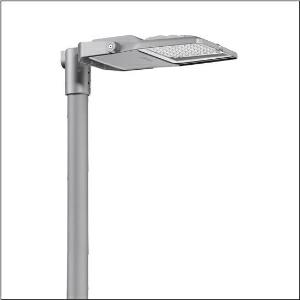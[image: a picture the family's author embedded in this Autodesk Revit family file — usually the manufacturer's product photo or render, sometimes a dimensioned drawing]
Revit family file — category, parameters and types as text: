
# Revit family: floodlight_fl_21_mini___pl33t_5xa7776d2f3a_276e
name_source: partatom
category: Lighting Fixtures
units: mm (PartAtom-declared; Revit-internal decimal feet)

## family parameters
Cut with Voids When Loaded = No
Host = Face
Light Source = No
Part Type = Normal
Room Calculation Point = No
Round Connector Dimension = Use Diameter
Shared = No

## types (1)
- --- (1 x LED, 17630 lm, 142.9 W, 3000K)
    Apparent Load = 143 VA
    CIE Flux Codes = 26 75 99 100 100
    Color Rendering = 70
    Color Temperature = 3000K
    Default Elevation = 1800 mm
    Description = Floodlight FL 21 mini, floodlight, primary light control with lens, of PMMA, primary optical cover: protective disc, of toughened safety glass, transparent, light distribution: PL33T, light emission: direct distribution, installation type: surface-mounted, LED, High Power LED, rated luminous flux: 17.630lm, luminous efficacy: 123lm/W, light colour: 730, colour temperature: 3000K, control: flexible luminous flux parameterisation, time-dependent luminous flux control, constant luminous flux control, overheat protection, presetting dimming logarithmic, with terminal, 6-pole, mains connection: 220..240V, AC, 50/60Hz, start of lifetime: 143W, end of service life: 151W, reduction: 63W, luminaire housing, of diecast aluminium, powder-coated, Siteco® metallic grey (DB 702S), corrosivity category C5 mid according to DIN EN ISO 12944, sealing non-destructively replaceable, please order mast flange separately, mast bracket, of steel, galvanised, powder-coated, Siteco® metallic grey (DB 702S), Smart Interface below and above, protection rating (complete): IP66, insulation class (complete): insulation class II (safety insulation), certification: CE, ENEC, VDE, protection symbol: D, impact resistance: IK08, permissible operating ambient temperature: -40..+40°C, permissible operating ambient temperature for outdoor applications: -40..+50°C, standard: DIN EN 12944, LABS conformity tested according to VDMA 24364:2018-05, packaging unit: 1 piece

Light Distribution: PL33T
    Height = 70 mm
    Lamp = 1 x LED
    Lamp Light Flux = 17630 lm
    Lamp Power = 142.9 W
    Lamp count = 1
    Length = 485 mm
    Luminous efficacy = 123 lm/W
    Manufacturer = Siteco
    ModVariant = No
    Model = 5XA7776D2F3A
    Number of Poles = 1
    OnlyDefault = Yes
    Power Factor = 1
    Product Name = Floodlight FL 21 mini | PL33T
    Product group = floodlight | pylon annexe
    ProductGroupID = 6200
    Protection Class = Protection class II
    Protection Degree = IP 66
    RLX_Detail_Level = 1
    RLX_Emergency_Light_Flux = 0 lm
    RLX_Emergency_Type = 0
    RLX_Emergency_Type_DB = No
    RlxData = <blob elided: 101129 chars, md5=d5a3c19a>
    Socket = socket
    Standby Power = 0 W
    System Light Flux = 17630 lm
    System Power = 143 W
    Type Comments = factory setting: luminous flux: 100 % | dim-lin: 254 | 730 mA
    Type Image = l_1007125.jpg
    URL = http://relux.com
    VarID = @adj_080817
    Voltage = 0 V
    Weight = 0.00 kg
    Width = 337 mm

## geometry (parser evidence)
native form markers: Blend x4, Sweep x12
no freeform markers — native parametric forms only
